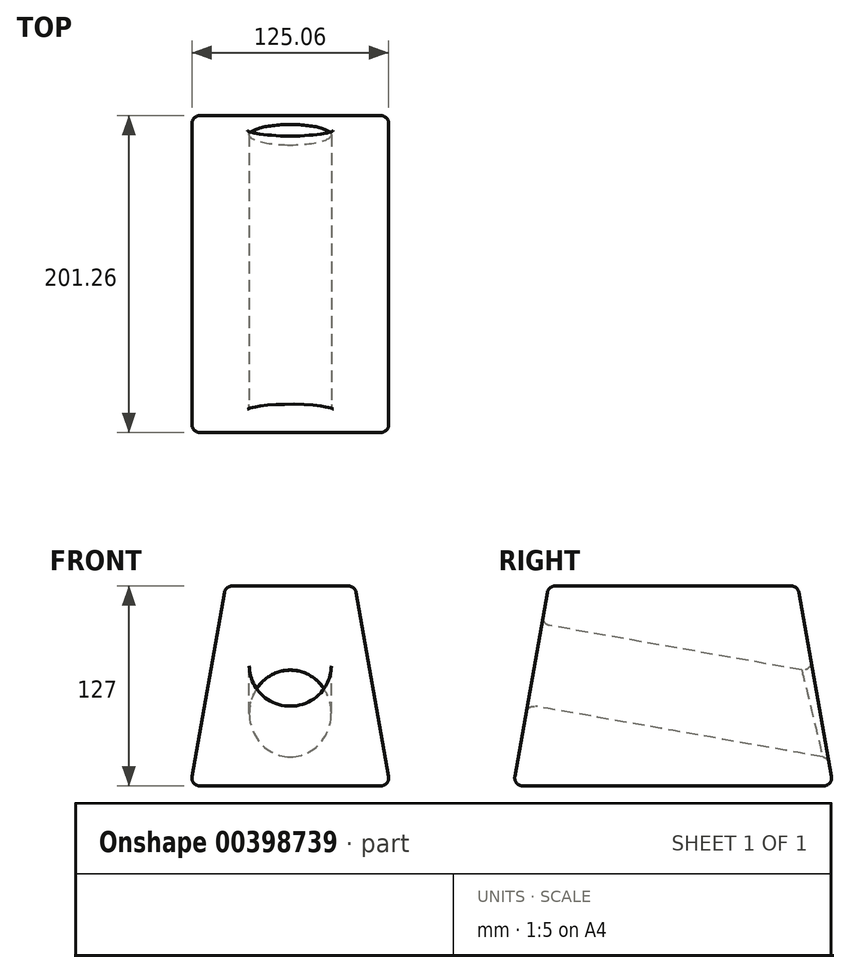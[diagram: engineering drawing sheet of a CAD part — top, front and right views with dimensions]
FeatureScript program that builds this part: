
annotation { "Feature Type Name" : "Feature", "Feature Type Description" : "" }
export const myFeature = defineFeature(function(context is Context, id is Id, definition is map)
    precondition{}
    {
        {
            var Q0;
            Q0=qCreatedBy(makeId("Top.planeOp"),FACE);
            var sketch = newSketch(context, id + "F0", { "sketchPlane" : qUnion([Q0])});
            skLineSegment(sketch, "E0.bottom", {"start": v(-50.8, 76.2) * mm, "end": v(76.2, 76.2) * mm});
            skLineSegment(sketch, "E0.top", {"start": v(-50.8, -127) * mm, "end": v(76.2, -127) * mm});
            skLineSegment(sketch, "E0.left", {"start": v(-50.8, 76.2) * mm, "end": v(-50.8, -127) * mm});
            skLineSegment(sketch, "E0.right", {"start": v(76.2, 76.2) * mm, "end": v(76.2, -127) * mm});
            skLineSegment(sketch, "E1", {"start": v(0, 0) * mm, "end": v(0, 76.2) * mm, "construction": true});
            skLineSegment(sketch, "E2", {"start": v(0, 0) * mm, "end": v(-50.8, 0) * mm, "construction": true});
            skSolve(sketch);
        }
        {
            var Q0;
            Q0 = qSketchRegion(id + "F0", true);
            extrude(context, id + "F1", {"entities" : qUnion([Q0]), "depth" : 127 * mm, "hasDraft" : true, "draftAngle" : 10 * degree, "draftPullDirection" : true});
        }
        {
            var Q0;
            Q0=makeQuery(id+"F1.opExtrude","SWEPT_FACE",FACE,{"disambiguationData":[OSD([sQuery(id+"F0.wireOp",EDGE,"E0.top")])]});
            var sketch = newSketch(context, id + "F2", { "sketchPlane" : qUnion([Q0])});
            skLineSegment(sketch, "E3", {"start": v(-28.4, 106.9) * mm, "end": v(76.2, -22.05) * mm, "construction": true});
            skLineSegment(sketch, "E4", {"start": v(53.8, 106.9) * mm, "end": v(-50.8, -22.05) * mm, "construction": true});
            skPoint(sketch, "E5", {"position": v(12.7, 56.23) * mm});
            skSolve(sketch);
        }
        {
            var Q0;
            Q0=sQuery(id+"F2.wireOp",VERTEX,"E5");
            var Q1;
            Q1=makeQuery(id+"F1.opExtrude","SWEPT_BODY",BODY,{"disambiguationData":[OSD([sQuery(id+"F0.wireOp",EDGE,"E0.bottom"),sQuery(id+"F0.wireOp",EDGE,"E0.top"),sQuery(id+"F0.wireOp",EDGE,"E0.left"),sQuery(id+"F0.wireOp",EDGE,"E0.right")])]});
            hole(context, id + "F3", {"style" : HoleStyle.SIMPLE, "endStyle" : HoleEndStyle.THROUGH, "holeDiameter" : 52.07 * mm, "isTappedThrough" : true, "tappedDepth" : 12.7 * mm, "tapClearance" : 3, "startFromSketch" : true, "locations" : qUnion([Q0]), "scope" : qUnion([Q1])});
        }
        {
            var Q0;
            Q0=makeQuery(id+"F1.opExtrude","SWEPT_FACE",FACE,{"disambiguationData":[OSD([sQuery(id+"F0.wireOp",EDGE,"E0.top")])]});
            var Q1;
            Q1=makeQuery(id+"F1.opExtrude","SWEPT_FACE",FACE,{"disambiguationData":[OSD([sQuery(id+"F0.wireOp",EDGE,"E0.bottom")])]});
            var Q2;
            Q2=makeQuery(id+"F1.opExtrude","CAP_FACE",FACE,{"disambiguationData":[OSD([sQuery(id+"F0.wireOp",EDGE,"E0.bottom"),sQuery(id+"F0.wireOp",EDGE,"E0.top"),sQuery(id+"F0.wireOp",EDGE,"E0.left"),sQuery(id+"F0.wireOp",EDGE,"E0.right")])],"isStart":false});
            var Q3;
            Q3=makeQuery(id+"F1.opExtrude","SWEPT_FACE",FACE,{"disambiguationData":[OSD([sQuery(id+"F0.wireOp",EDGE,"E0.right")])]});
            var Q4;
            Q4=makeQuery(id+"F1.opExtrude","SWEPT_FACE",FACE,{"disambiguationData":[OSD([sQuery(id+"F0.wireOp",EDGE,"E0.left")])]});
            fillet(context, id + "F4", {"entities" : qUnion([Q0, Q1, Q2, Q3, Q4]), "radius" : 5.08 * mm, "tangentPropagation" : true, "allowEdgeOverflow" : false});
        }
    });
